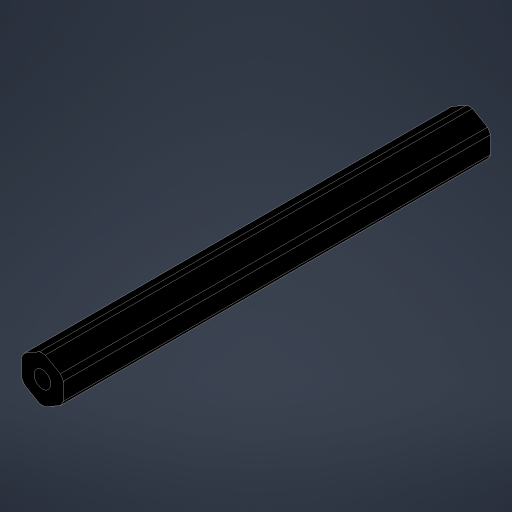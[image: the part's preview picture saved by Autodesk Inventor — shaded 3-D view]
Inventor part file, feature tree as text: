
AUTODESK INVENTOR PART (.ipt)
format: ipt  version: 2023.4 (Build 274418000, 418)  size: 192,000 bytes
history: native  units: in
note: dims shown in document units (in); Inventor stores cm internally (conversion verified against a paired STEP export)
features: extrude x2, projected_geometry x2, hole x1
ambient origin geometry x8: Origin, YZ Plane, XZ Plane, XY Plane, X Axis, Y Axis, Z Axis, Center Point
bodies: Solid1 (feature_tree)
feature tree (5):
  extrude  "Extrusion1"  TaperAngle=0.0deg  [1 undecoded]
  hole  "Hole1"  [1 undecoded]
  extrude  "Extrusion3"  TaperAngle=0.0deg  [1 undecoded]
  projected_geometry  "Project Cut Edges1"
  projected_geometry  "Project Cut Edges2"
note: 3 required parameter values undecoded (feature->parameter linkage not recoverable at this tier; creation-order binding heuristic only, values carry confidence <= 0.55)
